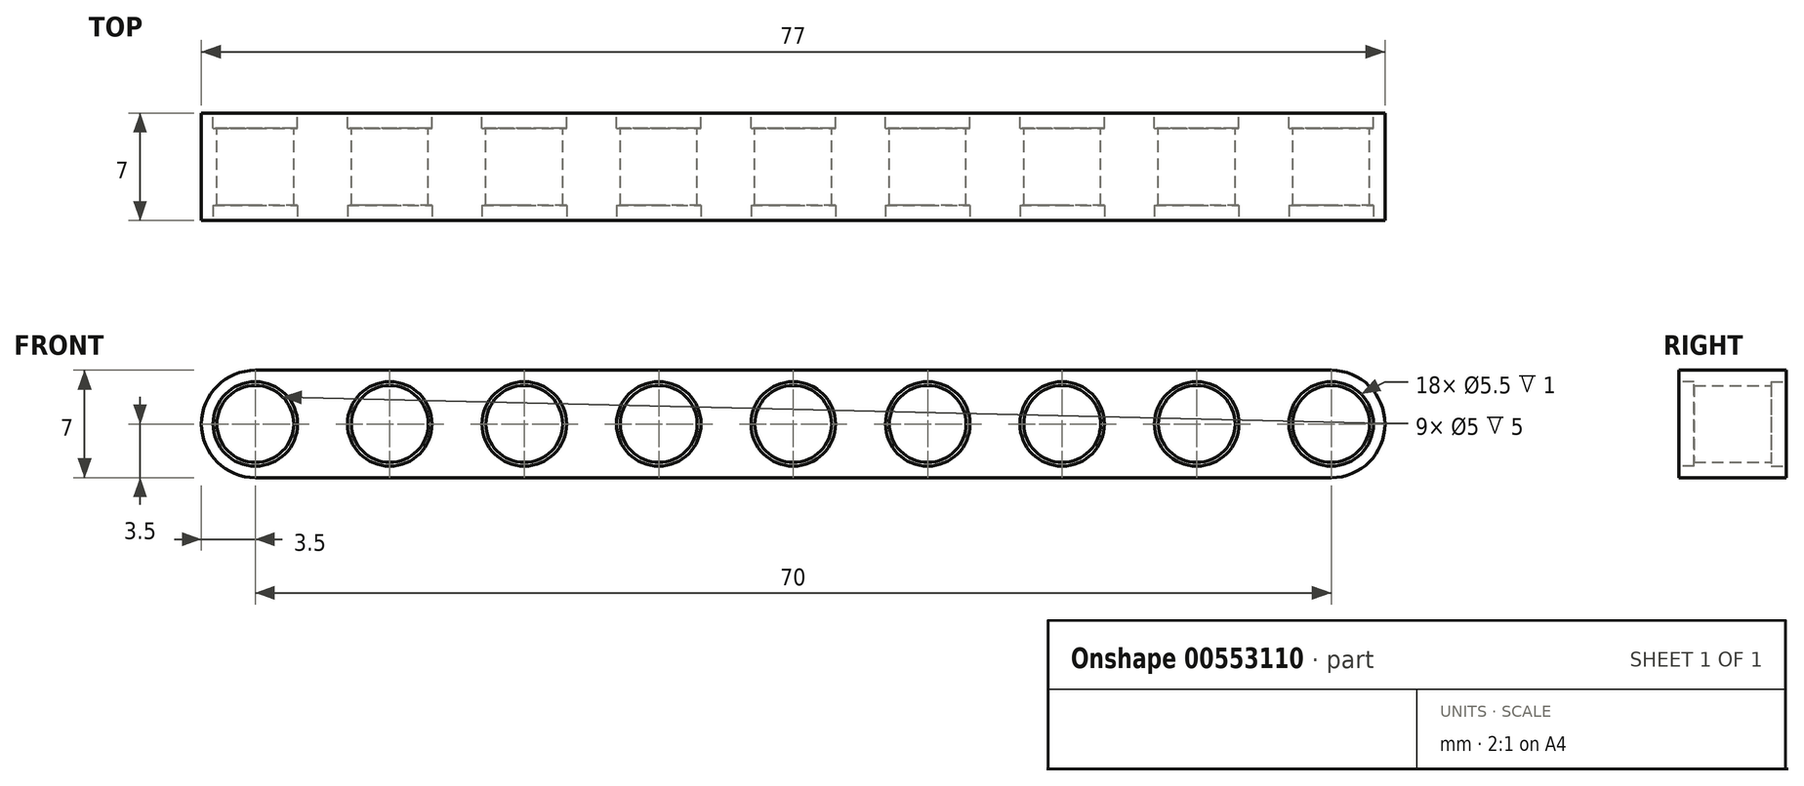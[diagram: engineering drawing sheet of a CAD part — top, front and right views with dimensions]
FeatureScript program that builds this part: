
annotation { "Feature Type Name" : "Feature", "Feature Type Description" : "" }
export const myFeature = defineFeature(function(context is Context, id is Id, definition is map)
    precondition{}
    {
        {
            var Q0;
            Q0=qCreatedBy(makeId("Front.planeOp"),FACE);
            var sketch = newSketch(context, id + "F0", { "sketchPlane" : qUnion([Q0])});
            skLineSegment(sketch, "E0.bottom", {"start": v(35, 3.5) * mm, "end": v(-35, 3.5) * mm});
            skLineSegment(sketch, "E0.top", {"start": v(35, -3.5) * mm, "end": v(-35, -3.5) * mm});
            skPoint(sketch, "E0.middle", {"position": v(0, 0) * mm});
            skArc(sketch, "E1", {"start": v(-35, 3.5) * mm, "mid": v(-38.5, 0) * mm, "end": v(-35, -3.5) * mm});
            skArc(sketch, "E2", {"start": v(35, -3.5) * mm, "mid": v(38.5, 0) * mm, "end": v(35, 3.5) * mm});
            skCircle(sketch, "E3", {"center": v(-35, 0) * mm, "radius": 2.5 * mm});
            skCircle(sketch, "E4.1.0.0", {"center": v(-26.25, 0) * mm, "radius": 2.5 * mm});
            skCircle(sketch, "E4.2.0.0", {"center": v(-17.5, 0) * mm, "radius": 2.5 * mm});
            skCircle(sketch, "E4.3.0.0", {"center": v(-8.75, 0) * mm, "radius": 2.5 * mm});
            skCircle(sketch, "E4.4.0.0", {"center": v(0, 0) * mm, "radius": 2.5 * mm});
            skCircle(sketch, "E4.5.0.0", {"center": v(8.75, 0) * mm, "radius": 2.5 * mm});
            skCircle(sketch, "E4.6.0.0", {"center": v(17.5, 0) * mm, "radius": 2.5 * mm});
            skCircle(sketch, "E4.7.0.0", {"center": v(26.25, 0) * mm, "radius": 2.5 * mm});
            skCircle(sketch, "E4.8.0.0", {"center": v(35, 0) * mm, "radius": 2.5 * mm});
            skLineSegment(sketch, "E4.direction1", {"start": v(-35, 0) * mm, "end": v(-26.25, 0) * mm, "construction": true});
            skSolve(sketch);
        }
        {
            var Q0;
            Q0 = qSketchRegion(id + "F0", true);
            extrude(context, id + "F1", {"entities" : qUnion([Q0]), "depth" : 7 * mm, "offsetDistance" : 25 * mm});
        }
        {
            var Q0;
            Q0=makeQuery(id+"F1.opExtrude","CAP_FACE",FACE,{"disambiguationData":[OSD([sQuery(id+"F0.wireOp",EDGE,"E0.bottom"),sQuery(id+"F0.wireOp",EDGE,"E0.top"),sQuery(id+"F0.wireOp",EDGE,"E1"),sQuery(id+"F0.wireOp",EDGE,"E2"),sQuery(id+"F0.wireOp",EDGE,"E3"),sQuery(id+"F0.wireOp",EDGE,"E4.1.0.0"),sQuery(id+"F0.wireOp",EDGE,"E4.2.0.0"),sQuery(id+"F0.wireOp",EDGE,"E4.3.0.0"),sQuery(id+"F0.wireOp",EDGE,"E4.4.0.0"),sQuery(id+"F0.wireOp",EDGE,"E4.5.0.0"),sQuery(id+"F0.wireOp",EDGE,"E4.6.0.0"),sQuery(id+"F0.wireOp",EDGE,"E4.7.0.0"),sQuery(id+"F0.wireOp",EDGE,"E4.8.0.0")])],"isStart":false});
            var sketch = newSketch(context, id + "F2", { "sketchPlane" : qUnion([Q0])});
            skCircle(sketch, "E5", {"center": v(35, 0) * mm, "radius": 2.75 * mm});
            skCircle(sketch, "E6.1.0.0", {"center": v(26.25, 0) * mm, "radius": 2.75 * mm});
            skCircle(sketch, "E6.2.0.0", {"center": v(17.5, 0) * mm, "radius": 2.75 * mm});
            skCircle(sketch, "E6.3.0.0", {"center": v(8.75, 0) * mm, "radius": 2.75 * mm});
            skCircle(sketch, "E6.4.0.0", {"center": v(0, 0) * mm, "radius": 2.75 * mm});
            skCircle(sketch, "E6.5.0.0", {"center": v(-8.75, 0) * mm, "radius": 2.75 * mm});
            skCircle(sketch, "E6.6.0.0", {"center": v(-17.5, 0) * mm, "radius": 2.75 * mm});
            skCircle(sketch, "E6.7.0.0", {"center": v(-26.25, 0) * mm, "radius": 2.75 * mm});
            skCircle(sketch, "E6.8.0.0", {"center": v(-35, 0) * mm, "radius": 2.75 * mm});
            skLineSegment(sketch, "E6.direction1", {"start": v(35, 0) * mm, "end": v(26.25, 0) * mm, "construction": true});
            skSolve(sketch);
        }
        {
            var Q0;
            Q0 = qSketchRegion(id + "F2", true);
            extrude(context, id + "F3", {"entities" : qUnion([Q0]), "operationType" : NewBodyOperationType.REMOVE, "oppositeDirection" : true, "depth" : 1 * mm, "offsetDistance" : 25 * mm});
        }
        {
            var Q0;
            Q0=makeQuery(id+"F1.opExtrude","CAP_FACE",FACE,{"disambiguationData":[OSD([sQuery(id+"F0.wireOp",EDGE,"E0.bottom"),sQuery(id+"F0.wireOp",EDGE,"E0.top"),sQuery(id+"F0.wireOp",EDGE,"E1"),sQuery(id+"F0.wireOp",EDGE,"E2"),sQuery(id+"F0.wireOp",EDGE,"E3"),sQuery(id+"F0.wireOp",EDGE,"E4.1.0.0"),sQuery(id+"F0.wireOp",EDGE,"E4.2.0.0"),sQuery(id+"F0.wireOp",EDGE,"E4.3.0.0"),sQuery(id+"F0.wireOp",EDGE,"E4.4.0.0"),sQuery(id+"F0.wireOp",EDGE,"E4.5.0.0"),sQuery(id+"F0.wireOp",EDGE,"E4.6.0.0"),sQuery(id+"F0.wireOp",EDGE,"E4.7.0.0"),sQuery(id+"F0.wireOp",EDGE,"E4.8.0.0")])],"isStart":true});
            var sketch = newSketch(context, id + "F4", { "sketchPlane" : qUnion([Q0])});
            skCircle(sketch, "E7", {"center": v(35, 0) * mm, "radius": 2.75 * mm});
            skCircle(sketch, "E8.1.0.0", {"center": v(26.25, 0) * mm, "radius": 2.75 * mm});
            skCircle(sketch, "E8.2.0.0", {"center": v(17.5, 0) * mm, "radius": 2.75 * mm});
            skCircle(sketch, "E8.3.0.0", {"center": v(8.75, 0) * mm, "radius": 2.75 * mm});
            skCircle(sketch, "E8.4.0.0", {"center": v(0, 0) * mm, "radius": 2.75 * mm});
            skCircle(sketch, "E8.5.0.0", {"center": v(-8.75, 0) * mm, "radius": 2.75 * mm});
            skCircle(sketch, "E8.6.0.0", {"center": v(-17.5, 0) * mm, "radius": 2.75 * mm});
            skCircle(sketch, "E8.7.0.0", {"center": v(-26.25, 0) * mm, "radius": 2.75 * mm});
            skCircle(sketch, "E8.8.0.0", {"center": v(-35, 0) * mm, "radius": 2.75 * mm});
            skLineSegment(sketch, "E8.direction1", {"start": v(35, 0) * mm, "end": v(26.25, 0) * mm, "construction": true});
            skSolve(sketch);
        }
        {
            var Q0;
            Q0 = qSketchRegion(id + "F4", true);
            extrude(context, id + "F5", {"entities" : qUnion([Q0]), "operationType" : NewBodyOperationType.REMOVE, "oppositeDirection" : true, "depth" : 1 * mm, "offsetDistance" : 25 * mm});
        }
    });
